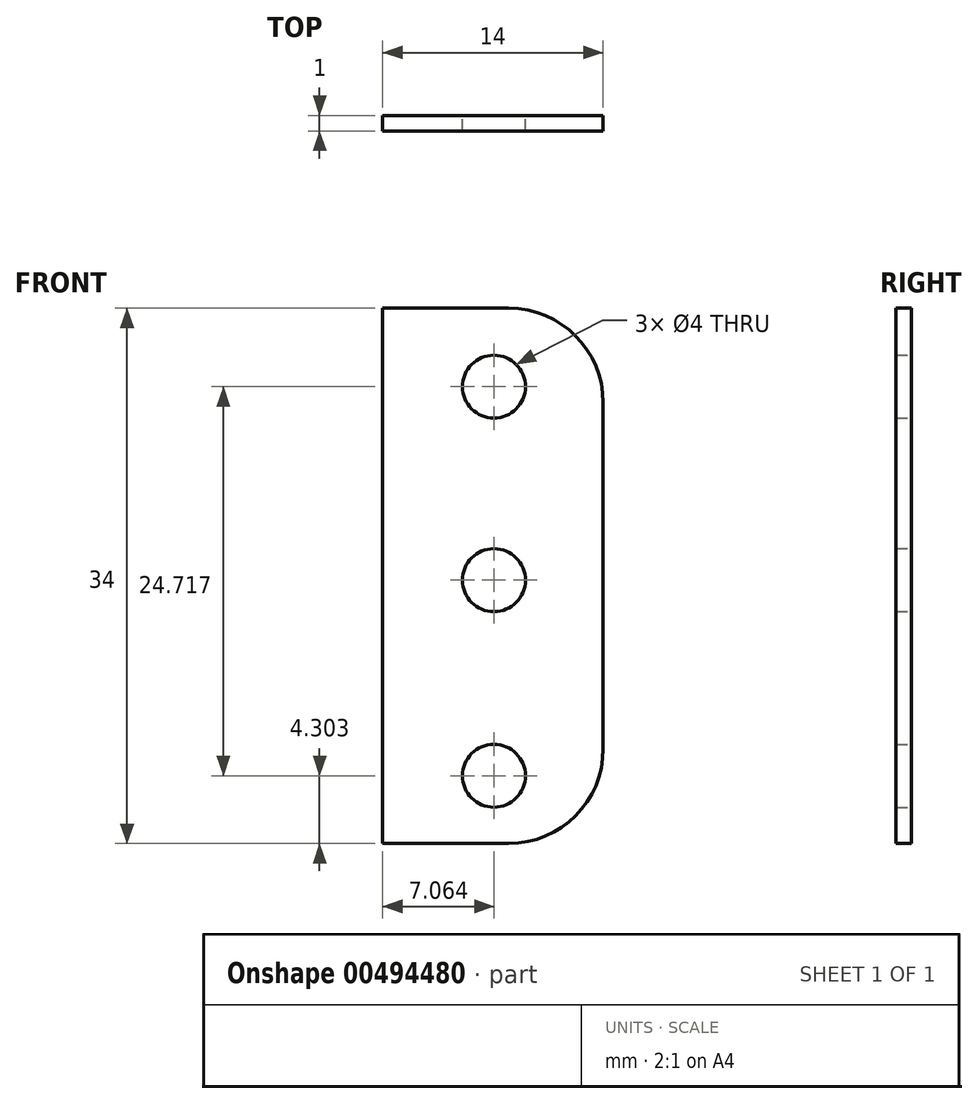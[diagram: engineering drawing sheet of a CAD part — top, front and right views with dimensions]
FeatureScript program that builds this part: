
annotation { "Feature Type Name" : "Feature", "Feature Type Description" : "" }
export const myFeature = defineFeature(function(context is Context, id is Id, definition is map)
    precondition{}
    {
        {
            var Q0;
            Q0=qCreatedBy(makeId("Front.planeOp"),FACE);
            var sketch = newSketch(context, id + "F0", { "sketchPlane" : qUnion([Q0])});
            skLineSegment(sketch, "E0", {"start": v(-30.19, -13.94) * mm, "end": v(-30.19, 20.06) * mm});
            skLineSegment(sketch, "E1", {"start": v(-30.19, 20.06) * mm, "end": v(-22.19, 20.06) * mm});
            skLineSegment(sketch, "E2", {"start": v(-16.19, 14.06) * mm, "end": v(-16.19, -7.94) * mm});
            skLineSegment(sketch, "E3", {"start": v(-22.19, -13.94) * mm, "end": v(-30.19, -13.94) * mm});
            skPoint(sketch, "E4.visualSharp", {"position": v(-16.19, 20.06) * mm});
            skArc(sketch, "E4.filletArc", {"start": v(-16.19, 14.06) * mm, "mid": v(-17.94, 18.3) * mm, "end": v(-22.19, 20.06) * mm});
            skPoint(sketch, "E5.visualSharp", {"position": v(-16.19, -13.94) * mm});
            skArc(sketch, "E5.filletArc", {"start": v(-22.19, -13.94) * mm, "mid": v(-17.94, -12.18) * mm, "end": v(-16.19, -7.94) * mm});
            skCircle(sketch, "E6", {"center": v(-23.13, 15.08) * mm, "radius": 2 * mm});
            skCircle(sketch, "E7", {"center": v(-23.13, 2.79) * mm, "radius": 2 * mm});
            skCircle(sketch, "E8", {"center": v(-23.13, -9.64) * mm, "radius": 2 * mm});
            skSolve(sketch);
        }
        {
            var Q0;
            Q0=makeQuery(id+"F0.imprint","IMPRINT",FACE,{"disambiguationData":[TD([[makeQuery(id+"F0.imprint","IMPRINT",EDGE,{"derivedFrom":sQuery(id+"F0.wireOp",EDGE,"E0")}),-1.0]])]});
            extrude(context, id + "F1", {"entities" : qUnion([Q0]), "depth" : 1 * mm});
        }
    });
